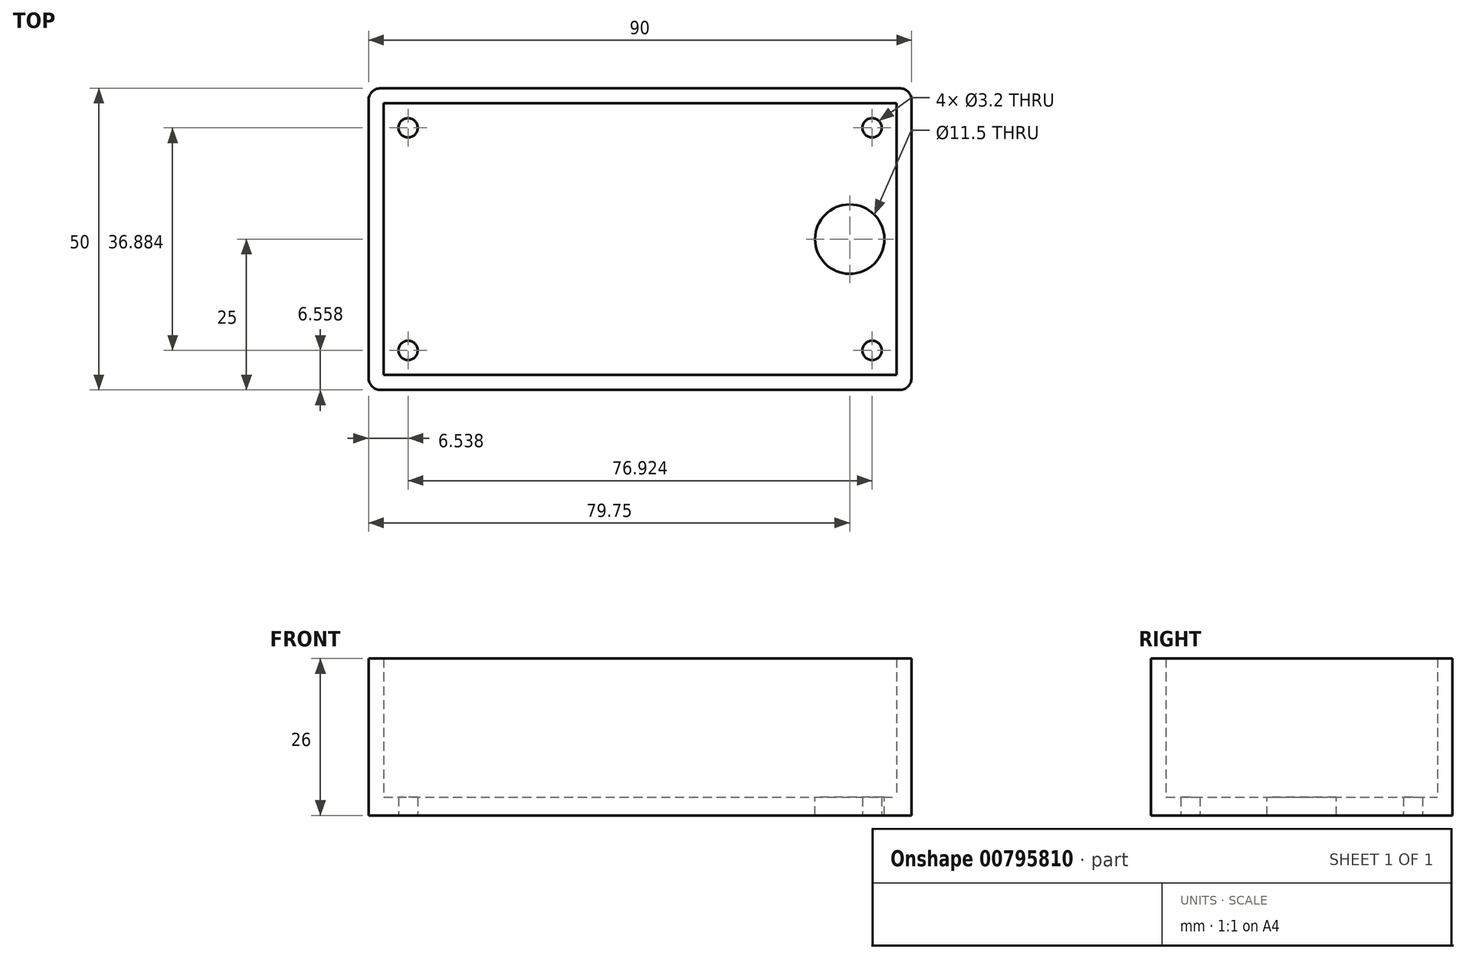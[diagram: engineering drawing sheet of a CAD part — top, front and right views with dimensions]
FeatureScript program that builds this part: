
annotation { "Feature Type Name" : "Feature", "Feature Type Description" : "" }
export const myFeature = defineFeature(function(context is Context, id is Id, definition is map)
    precondition{}
    {
        {
            var Q0;
            Q0=qCreatedBy(makeId("Top.planeOp"),FACE);
            var sketch = newSketch(context, id + "F0", { "sketchPlane" : qUnion([Q0])});
            skLineSegment(sketch, "E0.bottom", {"start": v(42.5, 22.5) * mm, "end": v(-42.5, 22.5) * mm});
            skLineSegment(sketch, "E0.top", {"start": v(42.5, -22.5) * mm, "end": v(-42.5, -22.5) * mm});
            skLineSegment(sketch, "E0.left", {"start": v(42.5, 22.5) * mm, "end": v(42.5, -22.5) * mm});
            skLineSegment(sketch, "E0.right", {"start": v(-42.5, 22.5) * mm, "end": v(-42.5, -22.5) * mm});
            skPoint(sketch, "E0.middle", {"position": v(0, 0) * mm});
            skLineSegment(sketch, "E1.bottom", {"start": v(45, 25) * mm, "end": v(-45, 25) * mm});
            skLineSegment(sketch, "E1.top", {"start": v(45, -25) * mm, "end": v(-45, -25) * mm});
            skLineSegment(sketch, "E1.left", {"start": v(45, 25) * mm, "end": v(45, -25) * mm});
            skLineSegment(sketch, "E1.right", {"start": v(-45, 25) * mm, "end": v(-45, -25) * mm});
            skSolve(sketch);
        }
        {
            var Q0;
            Q0=makeQuery(id+"F0.imprint","IMPRINT",FACE,{"disambiguationData":[TD([[makeQuery(id+"F0.imprint","IMPRINT",EDGE,{"derivedFrom":sQuery(id+"F0.wireOp",EDGE,"E0.bottom")}),-1.0]])]});
            var Q1;
            Q1=makeQuery(id+"F0.imprint","IMPRINT",FACE,{"disambiguationData":[TD([[makeQuery(id+"F0.imprint","IMPRINT",EDGE,{"derivedFrom":sQuery(id+"F0.wireOp",EDGE,"E0.bottom")}),1.0]])]});
            extrude(context, id + "F1", {"entities" : qUnion([Q0, Q1]), "depth" : 3 * mm, "offsetDistance" : 25 * mm});
        }
        {
            var Q0;
            Q0=makeQuery(id+"F0.imprint","IMPRINT",FACE,{"disambiguationData":[TD([[makeQuery(id+"F0.imprint","IMPRINT",EDGE,{"derivedFrom":sQuery(id+"F0.wireOp",EDGE,"E0.bottom")}),-1.0]])]});
            extrude(context, id + "F2", {"entities" : qUnion([Q0]), "operationType" : NewBodyOperationType.ADD, "depth" : 26 * mm, "offsetDistance" : 25 * mm});
        }
        {
            var Q0;
            {var subQ0=sQuery(id+"F0.wireOp",EDGE,"E1.right");var subQ1=sQuery(id+"F0.wireOp",EDGE,"E1.top");Q0=makeQuery(id+"F2.boolean.opBoolean","MERGE",EDGE,{"derivedFrom":[makeQuery(id+"F1.opExtrude","SWEPT_EDGE",EDGE,{"disambiguationData":[OSD([subQ1,subQ0])]}),makeQuery(id+"F2.opExtrude","SWEPT_EDGE",EDGE,{"disambiguationData":[OSD([subQ1,subQ0])]})]});}
            var Q1;
            {var subQ0=sQuery(id+"F0.wireOp",EDGE,"E1.left");var subQ1=sQuery(id+"F0.wireOp",EDGE,"E1.top");Q1=makeQuery(id+"F2.boolean.opBoolean","MERGE",EDGE,{"derivedFrom":[makeQuery(id+"F1.opExtrude","SWEPT_EDGE",EDGE,{"disambiguationData":[OSD([subQ1,subQ0])]}),makeQuery(id+"F2.opExtrude","SWEPT_EDGE",EDGE,{"disambiguationData":[OSD([subQ1,subQ0])]})]});}
            var Q2;
            {var subQ0=sQuery(id+"F0.wireOp",EDGE,"E1.right");var subQ1=sQuery(id+"F0.wireOp",EDGE,"E1.bottom");Q2=makeQuery(id+"F2.boolean.opBoolean","MERGE",EDGE,{"derivedFrom":[makeQuery(id+"F1.opExtrude","SWEPT_EDGE",EDGE,{"disambiguationData":[OSD([subQ1,subQ0])]}),makeQuery(id+"F2.opExtrude","SWEPT_EDGE",EDGE,{"disambiguationData":[OSD([subQ1,subQ0])]})]});}
            var Q3;
            {var subQ0=sQuery(id+"F0.wireOp",EDGE,"E1.left");var subQ1=sQuery(id+"F0.wireOp",EDGE,"E1.bottom");Q3=makeQuery(id+"F2.boolean.opBoolean","MERGE",EDGE,{"derivedFrom":[makeQuery(id+"F1.opExtrude","SWEPT_EDGE",EDGE,{"disambiguationData":[OSD([subQ1,subQ0])]}),makeQuery(id+"F2.opExtrude","SWEPT_EDGE",EDGE,{"disambiguationData":[OSD([subQ1,subQ0])]})]});}
            fillet(context, id + "F3", {"entities" : qUnion([Q0, Q1, Q2, Q3]), "radius" : 2 * mm, "tangentPropagation" : true, "allowEdgeOverflow" : false});
        }
        {
            var Q0;
            Q0=makeQuery(id+"F1.opExtrude","CAP_FACE",FACE,{"disambiguationData":[OSD([sQuery(id+"F0.wireOp",EDGE,"E1.bottom"),sQuery(id+"F0.wireOp",EDGE,"E1.top"),sQuery(id+"F0.wireOp",EDGE,"E1.left"),sQuery(id+"F0.wireOp",EDGE,"E1.right")])],"isStart":false});
            var sketch = newSketch(context, id + "F4", { "sketchPlane" : qUnion([Q0])});
            skCircle(sketch, "E2", {"center": v(34.75, 0) * mm, "radius": 5.75 * mm});
            skSolve(sketch);
        }
        {
            var Q0;
            Q0=makeQuery(id+"F4.imprint","IMPRINT",FACE,{"disambiguationData":[TD([[makeQuery(id+"F4.imprint","IMPRINT",EDGE,{"derivedFrom":sQuery(id+"F4.wireOp",EDGE,"E2")}),1.0]])]});
            extrude(context, id + "F5", {"entities" : qUnion([Q0]), "operationType" : NewBodyOperationType.REMOVE, "endBound" : BoundingType.UP_TO_NEXT, "oppositeDirection" : true, "depth" : 25 * mm, "offsetDistance" : 25 * mm});
        }
        {
            var Q0;
            Q0=makeQuery(id+"F1.opExtrude","CAP_FACE",FACE,{"disambiguationData":[OSD([sQuery(id+"F0.wireOp",EDGE,"E1.bottom"),sQuery(id+"F0.wireOp",EDGE,"E1.top"),sQuery(id+"F0.wireOp",EDGE,"E1.left"),sQuery(id+"F0.wireOp",EDGE,"E1.right")])],"isStart":true});
            var sketch = newSketch(context, id + "F6", { "sketchPlane" : qUnion([Q0])});
            skCircle(sketch, "E3", {"center": v(-38.46, -18.44) * mm, "radius": 1.6 * mm});
            skCircle(sketch, "E4.MirrorC", {"center": v(-38.46, 18.44) * mm, "radius": 1.6 * mm});
            skCircle(sketch, "E5.MirrorC", {"center": v(38.46, 18.44) * mm, "radius": 1.6 * mm});
            skCircle(sketch, "E6.MirrorC", {"center": v(38.46, -18.44) * mm, "radius": 1.6 * mm});
            skSolve(sketch);
        }
        {
            var Q0;
            Q0=qSketchRegion(id+"F6",true);
            extrude(context, id + "F7", {"entities" : qUnion([Q0]), "operationType" : NewBodyOperationType.REMOVE, "oppositeDirection" : true, "depth" : 25 * mm, "offsetDistance" : 25 * mm});
        }
    });
